# Revit family: IS_Gusto_BD412_BIM_NL
name_source: partatom
category: Plumbing Fixtures
units: mm (PartAtom-declared; Revit-internal decimal feet)

## family parameters
Always vertical = No
Cut with Voids When Loaded = No
OmniClass Number = 23.45.55.17
OmniClass Title = Mixing Faucets
Part Type = Normal
Room Calculation Point = No
Round Connector Dimension = Use Diameter
Shared = No
Work Plane-Based = No

## types (1)
- BD412AA - Gusto slim sink mixer C square spout blue start - Chrome
    Accessories = https://www.idealstandard.nl
    Afmetingen = 139 x 239 x 424 mm
    AfstandsEenheid = Millimeter
    Afwerking = Chrom
    AreaUnits = millimetres
    Artikelnummer = BD412AA
    Artikelomschrijving = Gusto Slim Spültischmischer C quadratischer Auslauf blauer Start - Chrom
    Artikelreferentie = Gusto Slim Spültischmischer C quadratischer Auslauf blauer Start - Chrom
    AssetType = Fixed
    Auteur = Ideal Standard
    BIMObjectName = IS_IdealStandard_Sinktaps_Gusto_BD412
    BIMobject category = Taps & Mixers
    BIMobject category code = sanitary-taps-mixers
    BIMobject main category = Sanitary
    BIMobject main category code = sanitary
    BarCode = 3800861108610
    Barcode = 3800861108610
    Bedieningkraan = Einhebel
    Bedieningkraanwerk = Einhebel
    BeschrijvingBovenkantKraan = C quadratischer Auslauf
    Beschrijvinggarantie = Herstellergarantie
    Bestanddelen = https://www.idealstandard.nl
    BimObjectNaam = IS_IdealStandard_Sinktaps_Gusto_BD412
    Brand = Ideal Standard
    Brand url = http://www.idealstandard.nl
    Breedte = 138.776139
    BrutoGewicht = 0
    Category = Taps & Mixers
    Color = Chrome
    ConnectionType = Plumbing
    Cost = 0 $
    CurrencyUnit = €
    CurrentRevision = 1
    Date of publishing = 19/08/2022
    Description = Gusto slim sink mixer C square spout blue start - Chrome
    Diepte = 239 mm
    DurationUnit = Years
    DuurEenheid = Jahre
    Edition number = 1
    Eigenschappen = Slim Spültischmischer C quadratischer Auslauf blauer Start - Chrom
    ExpectedLife = 5
    FaucetFunction = Sink Mixer
    FaucetOperation = Single Lever Sink Mixer
    FaucetTopDescription = C Square Spoud
    FaucetType = Sink Mixer
    Features = Slim Sink mixer C square spout blue start - Chrome
    Finish = Chrome
    Functiekraanwerk = Küchenmischer
    GTIN code = https://3800861108610
    Garantieunits = Jahre
    Help = https://www.idealstandard.nl
    Hoogte = 424.003766124835
    Hulp = https://www.idealstandard.nl
    IFC Classification = Sanitary Terminal
    IfcExportAs = IfcValveType
    IfcExportType = FAUCET
    Installatieinstructies = https://www.idealstandard.nl
    Installation instructions = https://www.idealstandard.nl
    InstallationInstructions = https://www.idealstandard.nl
    Kleur = Chrom
    Lengte = 239 mm
    LinearUnits = millimetres
    MainColor = Chrome
    MaintenanceInformation = https://www.idealstandard.nl
    Manufacturer = Ideal Standard
    Manufacturer name = Ideal Standard
    ManufacturerURL = http://www.idealstandard.nl
    Masterformat 2014 Code = 22 41 16.16
    Masterformat 2014 Description = Residential Sink
    Materiaal = Messing
    Material = Brass
    Material main = Brass
    Merk = Ideal Standard
    Model = BD412AA
    ModelNumber = BD412AA
    ModelReference = Gusto slim sink mixer C square spout blue start
    NBS Reference Code = 45-35-70/345
    NBS Reference Description = Water supply fittings for sinks
    Name = Sinktaps_Gusto_BD412_IdealStandard
    NettWeight = 1.82 Kg
    Nettogewicht = 1.82
    NominalDepth = 239 mm
    NominalHeight = 424 mm  [stored 1.39108 ft]
    NominalLength = 239 mm
    NominalWidth = 139 mm
    Normen = Sinktaps_Gusto_BD412_IdealStandard
    OmniClass Code = 23-31 11 00
    OmniClass Description = Faucets
    OppervlakteEenheid = Millimeter
    PredefinedType = Taps & Mixers
    Product Guid = 9b66ed44-e195-483c-ba43-cea60a640249
    Product SKU = BD412
    Product certification = https://www.idealstandard.nl
    Product data url = https://bimobject.com
    Product family = Gusto
    Product group = Taps & Mixers
    Product name = GUSTO SLIM SINK MIXER C SQUARE SPOUT BLUE START
    Product url = https://www.idealstandard.nl
    ProductInformation = https://www.idealstandard.nl
    Productinformatie = https://www.idealstandard.nl
    QR code = http://bimobject.com
    Revisie = 1
    Shape = Cylindrical
    Size = 139 x 239 x 424 mm
    Space = Internal
    SpareParts = https://www.idealstandard.nl
    Technical description = https://www.idealstandard.nl
    Telefoonnummer = (0228) 521-580
    Toepassing = Küchenmischer
    Type Comments = Plumbing
    Typeconnectie = Installation
    Typekraanwerk = Einhebelmischer
    UNSPSC Code = 301815
    URL = https://www.idealstandard.nl
    Uniclass 2015 Code = Pr_40_20_87_82
    Uniclass 2015 Name = Sink manual water supply sets
    Uniclass2015Beschrijving = Sink manual water supply sets
    Uniclass2015Code = Pr_40_20_87_84
    Uniclass2015Referentie = Pr_40_20_87_82
    Uniclass2015Title = Sink taps
    Uniclass2015Version = v1.26
    Urlproducent = https://www.idealstandard.nl
    ValutaEenheid = Euro
    Versie = 1
    Version = 1
    Vervangingskosten = 0
    VolumeUnits = Liters
    Volumeunits = Liter
    Vorm = Zylinder
    WRASURL = https://www.wrasapprovals.co.uk
    WarrantyDescription = manufacturer warranty
    WarrantyDurationParts = 5
    WarrantyDurationUnit = Years
    WarrantyStartDate = 19/08/2022
    Weight Net (Kg) = 1.82
    Wisselstukken = https://www.idealstandard.nl
    Youtube clip = https://www.youtube.com

note: [stored X ft] marks values corroborated as IEEE doubles in the binary element streams (Revit-internal decimal feet)

## geometry (parser evidence)
native form markers: Sweep x2
no freeform markers — native parametric forms only
